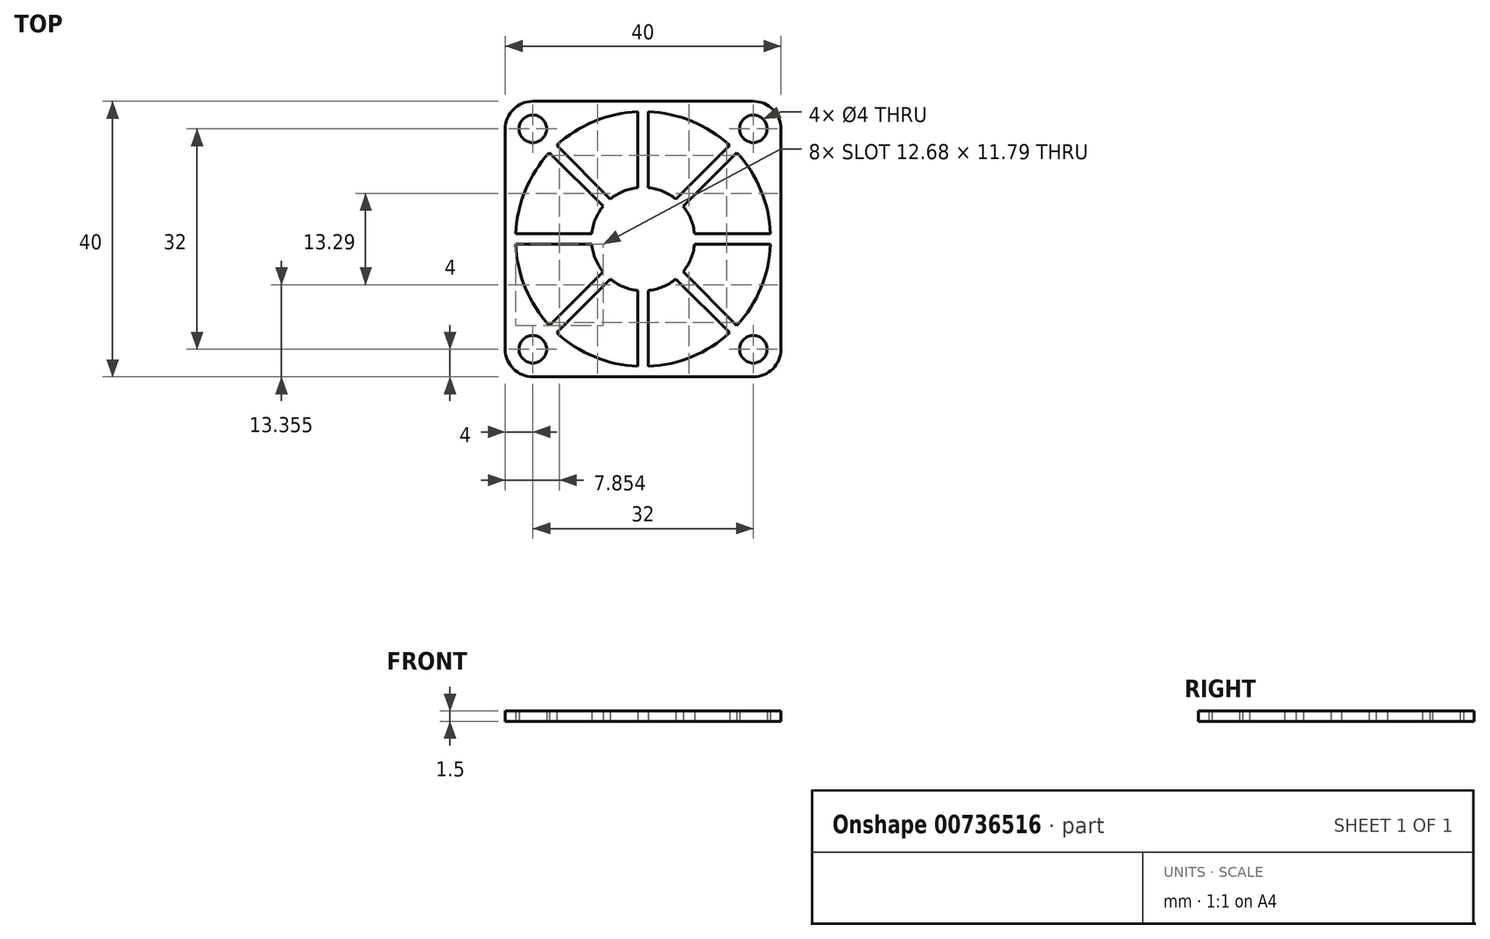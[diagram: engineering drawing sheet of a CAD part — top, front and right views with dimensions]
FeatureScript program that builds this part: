
annotation { "Feature Type Name" : "Feature", "Feature Type Description" : "" }
export const myFeature = defineFeature(function(context is Context, id is Id, definition is map)
    precondition{}
    {
        {
            var Q0;
            Q0=qCreatedBy(makeId("Top.planeOp"),FACE);
            var sketch = newSketch(context, id + "F0", { "sketchPlane" : qUnion([Q0])});
            skLineSegment(sketch, "E0.bottom", {"start": v(-20, 20) * mm, "end": v(20, 20) * mm});
            skLineSegment(sketch, "E0.top", {"start": v(-20, -20) * mm, "end": v(20, -20) * mm});
            skLineSegment(sketch, "E0.left", {"start": v(-20, 20) * mm, "end": v(-20, -20) * mm});
            skLineSegment(sketch, "E0.right", {"start": v(20, 20) * mm, "end": v(20, -20) * mm});
            skCircle(sketch, "E1", {"center": v(16, 16) * mm, "radius": 2 * mm});
            skCircle(sketch, "E2", {"center": v(-16, 16) * mm, "radius": 2 * mm});
            skCircle(sketch, "E3", {"center": v(-16, -16) * mm, "radius": 2 * mm});
            skCircle(sketch, "E4", {"center": v(16, -16) * mm, "radius": 2 * mm});
            skSolve(sketch);
        }
        {
            var Q0;
            Q0=qSketchRegion(id+"F0",true);
            extrude(context, id + "F1", {"entities" : qUnion([Q0]), "depth" : 1.5 * mm});
        }
        {
            var Q0;
            Q0=qCreatedBy(makeId("Top.planeOp"),FACE);
            var sketch = newSketch(context, id + "F2", { "sketchPlane" : qUnion([Q0])});
            skLineSegment(sketch, "E5.0", {"start": v(-20, 20) * mm, "end": v(20, 20) * mm});
            skLineSegment(sketch, "E6.0", {"start": v(-20, 20) * mm, "end": v(-20, -20) * mm});
            skLineSegment(sketch, "E7.0", {"start": v(-20, -20) * mm, "end": v(20, -20) * mm});
            skLineSegment(sketch, "E8.0", {"start": v(20, 20) * mm, "end": v(20, -20) * mm});
            skLineSegment(sketch, "E9", {"start": v(0, 7.5) * mm, "end": v(0, 18.5) * mm, "construction": true});
            skLineSegment(sketch, "E10", {"start": v(-0.75, 18.48) * mm, "end": v(-0.75, 7.46) * mm});
            skLineSegment(sketch, "E11.MirrorCS", {"start": v(0.75, 18.48) * mm, "end": v(0.75, 7.46) * mm});
            skArc(sketch, "E12", {"start": v(-0.75, 18.48) * mm, "mid": v(-7.08, 17.1) * mm, "end": v(-12.54, 13.6) * mm});
            skArc(sketch, "E13", {"start": v(-0.75, 7.46) * mm, "mid": v(-2.87, 6.93) * mm, "end": v(-4.75, 5.8) * mm});
            skLineSegment(sketch, "E14.1.0", {"start": v(-13.6, 12.54) * mm, "end": v(-5.8, 4.75) * mm});
            skLineSegment(sketch, "E14.1.1", {"start": v(-12.54, 13.6) * mm, "end": v(-4.75, 5.8) * mm});
            skLineSegment(sketch, "E14.2.0", {"start": v(-18.48, -0.75) * mm, "end": v(-7.46, -0.75) * mm});
            skLineSegment(sketch, "E14.2.1", {"start": v(-18.48, 0.75) * mm, "end": v(-7.46, 0.75) * mm});
            skLineSegment(sketch, "E14.3.0", {"start": v(-12.54, -13.6) * mm, "end": v(-4.75, -5.8) * mm});
            skLineSegment(sketch, "E14.3.1", {"start": v(-13.6, -12.54) * mm, "end": v(-5.8, -4.75) * mm});
            skLineSegment(sketch, "E14.4.0", {"start": v(0.75, -18.48) * mm, "end": v(0.75, -7.46) * mm});
            skLineSegment(sketch, "E14.4.1", {"start": v(-0.75, -18.48) * mm, "end": v(-0.75, -7.46) * mm});
            skLineSegment(sketch, "E14.5.0", {"start": v(13.6, -12.54) * mm, "end": v(5.8, -4.75) * mm});
            skLineSegment(sketch, "E14.5.1", {"start": v(12.54, -13.6) * mm, "end": v(4.75, -5.8) * mm});
            skLineSegment(sketch, "E14.6.0", {"start": v(18.48, 0.75) * mm, "end": v(7.46, 0.75) * mm});
            skLineSegment(sketch, "E14.6.1", {"start": v(18.48, -0.75) * mm, "end": v(7.46, -0.75) * mm});
            skLineSegment(sketch, "E14.7.0", {"start": v(12.54, 13.6) * mm, "end": v(4.75, 5.8) * mm});
            skLineSegment(sketch, "E14.7.1", {"start": v(13.6, 12.54) * mm, "end": v(5.8, 4.75) * mm});
            skArc(sketch, "E15.trimOffspring", {"start": v(-5.8, 4.75) * mm, "mid": v(-2.87, -6.93) * mm, "end": v(7.46, -0.75) * mm});
            skArc(sketch, "E16.trimOffspring", {"start": v(-13.6, 12.54) * mm, "mid": v(-17.1, 7.08) * mm, "end": v(-18.48, 0.75) * mm});
            skArc(sketch, "E17.trimOffspring", {"start": v(4.75, 5.8) * mm, "mid": v(2.87, 6.93) * mm, "end": v(0.75, 7.46) * mm});
            skArc(sketch, "E18.trimOffspring", {"start": v(12.54, 13.6) * mm, "mid": v(7.08, 17.1) * mm, "end": v(0.75, 18.48) * mm});
            skArc(sketch, "E19.trimOffspring", {"start": v(18.48, 0.75) * mm, "mid": v(17.1, 7.08) * mm, "end": v(13.6, 12.54) * mm});
            skArc(sketch, "E20.trimOffspring", {"start": v(7.46, 0.75) * mm, "mid": v(6.93, 2.87) * mm, "end": v(5.8, 4.75) * mm});
            skArc(sketch, "E21.trimOffspring", {"start": v(13.6, -12.54) * mm, "mid": v(17.1, -7.08) * mm, "end": v(18.48, -0.75) * mm});
            skArc(sketch, "E22.trimOffspring", {"start": v(0.75, -18.48) * mm, "mid": v(7.08, -17.1) * mm, "end": v(12.54, -13.6) * mm});
            skArc(sketch, "E23.trimOffspring", {"start": v(-12.54, -13.6) * mm, "mid": v(-7.08, -17.1) * mm, "end": v(-0.75, -18.48) * mm});
            skArc(sketch, "E24.trimOffspring", {"start": v(-18.48, -0.75) * mm, "mid": v(-17.1, -7.08) * mm, "end": v(-13.6, -12.54) * mm});
            skSolve(sketch);
        }
        {
            var Q0;
            Q0=qSketchRegion(id+"F2",true);
            extrude(context, id + "F3", {"entities" : qUnion([Q0]), "operationType" : NewBodyOperationType.INTERSECT, "depth" : 25 * mm});
        }
        {
            var Q0;
            Q0=makeQuery(id+"F1.opExtrude","SWEPT_EDGE",EDGE,{"disambiguationData":[OSD([sQuery(id+"F0.wireOp",EDGE,"E0.bottom"),sQuery(id+"F0.wireOp",EDGE,"E0.left")])]});
            var Q1;
            Q1=makeQuery(id+"F1.opExtrude","SWEPT_EDGE",EDGE,{"disambiguationData":[OSD([sQuery(id+"F0.wireOp",EDGE,"E0.bottom"),sQuery(id+"F0.wireOp",EDGE,"E0.right")])]});
            var Q2;
            Q2=makeQuery(id+"F1.opExtrude","SWEPT_EDGE",EDGE,{"disambiguationData":[OSD([sQuery(id+"F0.wireOp",EDGE,"E0.top"),sQuery(id+"F0.wireOp",EDGE,"E0.left")])]});
            var Q3;
            Q3=makeQuery(id+"F1.opExtrude","SWEPT_EDGE",EDGE,{"disambiguationData":[OSD([sQuery(id+"F0.wireOp",EDGE,"E0.top"),sQuery(id+"F0.wireOp",EDGE,"E0.right")])]});
            fillet(context, id + "F4", {"entities" : qUnion([Q0, Q1, Q2, Q3]), "radius" : 4 * mm, "tangentPropagation" : true, "allowEdgeOverflow" : false});
        }
    });
